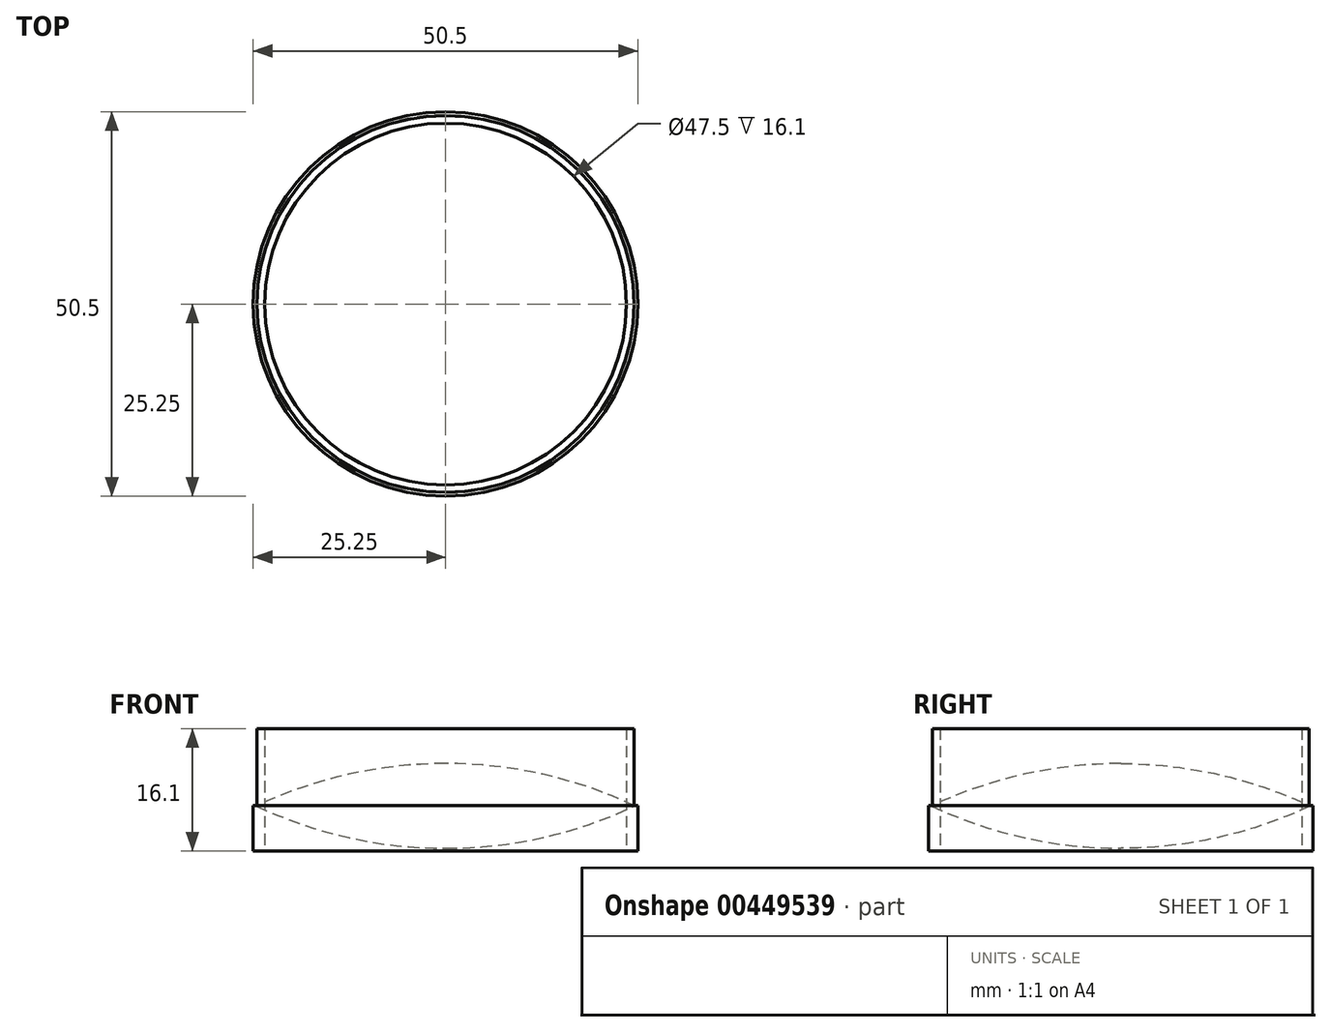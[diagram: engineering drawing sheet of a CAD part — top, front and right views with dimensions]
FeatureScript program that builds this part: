
annotation { "Feature Type Name" : "Feature", "Feature Type Description" : "" }
export const myFeature = defineFeature(function(context is Context, id is Id, definition is map)
    precondition{}
    {
        {
            var Q0;
            Q0=qCreatedBy(makeId("Top.planeOp"),FACE);
            var sketch = newSketch(context, id + "F0", { "sketchPlane" : qUnion([Q0])});
            skCircle(sketch, "E0", {"center": v(0, 0) * mm, "radius": 23.75 * mm});
            skCircle(sketch, "E1", {"center": v(0, 0) * mm, "radius": 24.75 * mm});
            skCircle(sketch, "E2", {"center": v(0, 0) * mm, "radius": 25.25 * mm});
            skSolve(sketch);
        }
        {
            var Q0;
            Q0=makeQuery(id+"F0.imprint","IMPRINT",FACE,{"disambiguationData":[TD([[makeQuery(id+"F0.imprint","IMPRINT",EDGE,{"derivedFrom":sQuery(id+"F0.wireOp",EDGE,"E0")}),-1.0]])]});
            extrude(context, id + "F1", {"entities" : qUnion([Q0]), "depth" : 16.1 * mm});
        }
        {
            var Q0;
            Q0=makeQuery(id+"F0.imprint","IMPRINT",FACE,{"disambiguationData":[TD([[makeQuery(id+"F0.imprint","IMPRINT",EDGE,{"derivedFrom":sQuery(id+"F0.wireOp",EDGE,"E1")}),-1.0]])]});
            extrude(context, id + "F2", {"entities" : qUnion([Q0]), "operationType" : NewBodyOperationType.ADD, "depth" : 6 * mm});
        }
        {
            var Q0;
            Q0=qCreatedBy(makeId("Right.planeOp"),FACE);
            var sketch = newSketch(context, id + "F3", { "sketchPlane" : qUnion([Q0])});
            skArc(sketch, "E3", {"start": v(24.85, 5.92) * mm, "mid": v(0, 11.49) * mm, "end": v(-24.85, 5.92) * mm});
            skArc(sketch, "E4", {"start": v(24.85, 5.92) * mm, "mid": v(0, 0.36) * mm, "end": v(-24.85, 5.92) * mm});
            skLineSegment(sketch, "E5", {"start": v(0, -16.47) * mm, "end": v(0, 49.7) * mm});
            skSolve(sketch);
        }
        {
            var Q0;
            {var subQ0=sQuery(id+"F3.wireOp",EDGE,"E4");var subQ1=sQuery(id+"F3.wireOp",EDGE,"E3");var subQ2=makeQuery(id+"F3.imprint","INTERSECT",VERTEX,{"disambiguationData":[OD(0.0)],"derivedFrom":[subQ1,subQ0]});Q0=makeQuery(id+"F3.imprint","IMPRINT",FACE,{"disambiguationData":[TD([[makeQuery(id+"F3.imprint","IMPRINT",EDGE,{"disambiguationData":[TD([[subQ2,-1.0]])],"derivedFrom":subQ1}),1.0]])]});}
            var Q1;
            Q1=sQuery(id+"F3.wireOp",EDGE,"E4");
            var Q2;
            Q2=sQuery(id+"F3.wireOp",EDGE,"E3");
            var Q3;
            Q3=sQuery(id+"F3.wireOp",EDGE,"E5");
            revolve(context, id + "F4", {"entities" : qUnion([Q0]), "surfaceEntities" : qUnion([Q1, Q2]), "axis" : qUnion([Q3]), "revolveType" : RevolveType.ONE_DIRECTION, "angle" : 360 * degree});
        }
    });
